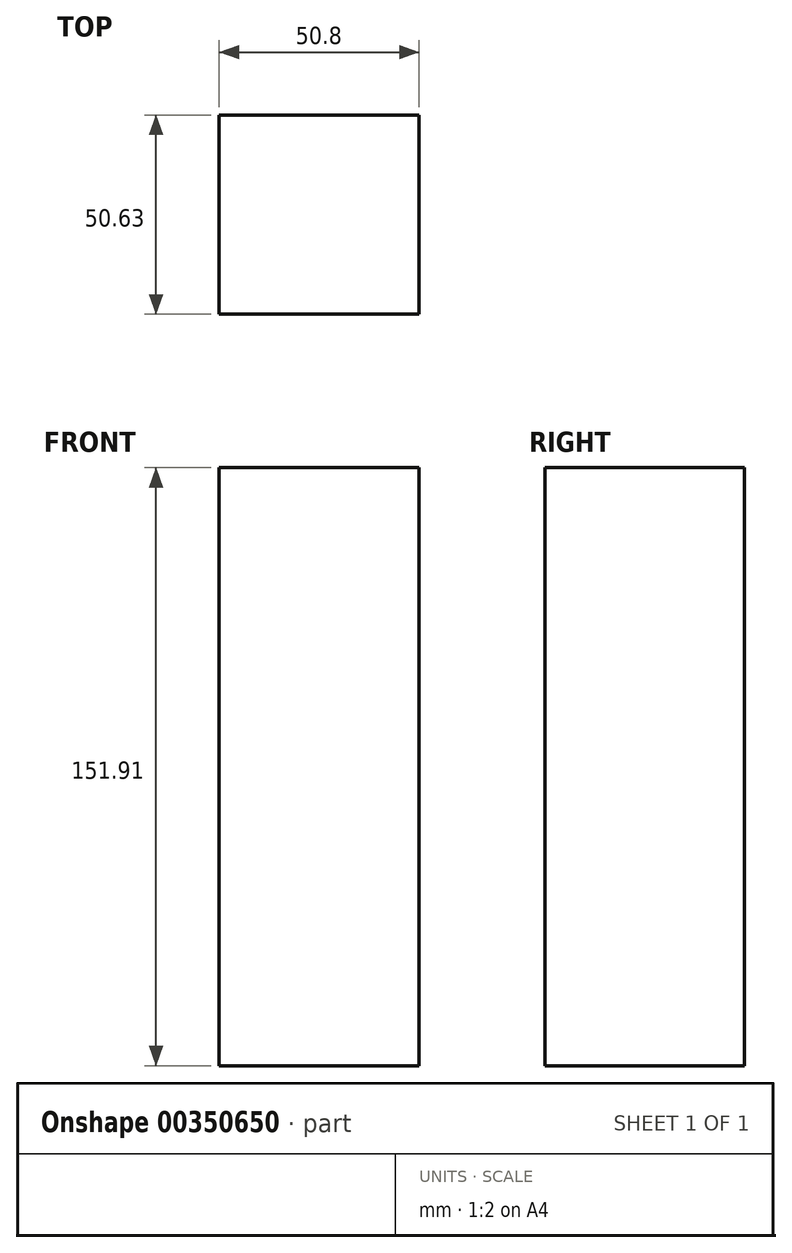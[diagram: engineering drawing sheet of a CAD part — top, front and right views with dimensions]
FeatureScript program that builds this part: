
annotation { "Feature Type Name" : "Feature", "Feature Type Description" : "" }
export const myFeature = defineFeature(function(context is Context, id is Id, definition is map)
    precondition{}
    {
        {
            var Q0;
            Q0=qCreatedBy(makeId("Right.planeOp"),FACE);
            var sketch = newSketch(context, id + "F0", { "sketchPlane" : qUnion([Q0])});
            skLineSegment(sketch, "E0.bottom", {"start": v(28.94, 74.98) * mm, "end": v(-21.7, 74.98) * mm});
            skLineSegment(sketch, "E0.top", {"start": v(28.94, -76.93) * mm, "end": v(-21.7, -76.93) * mm});
            skLineSegment(sketch, "E0.left", {"start": v(28.94, 74.98) * mm, "end": v(28.94, -76.93) * mm});
            skLineSegment(sketch, "E0.right", {"start": v(-21.7, 74.98) * mm, "end": v(-21.7, -76.93) * mm});
            skSolve(sketch);
        }
        {
            var Q0;
            Q0 = qSketchRegion(id + "F0", true);
            extrude(context, id + "F1", {"entities" : qUnion([Q0]), "depth" : 50.8 * mm});
        }
    });
